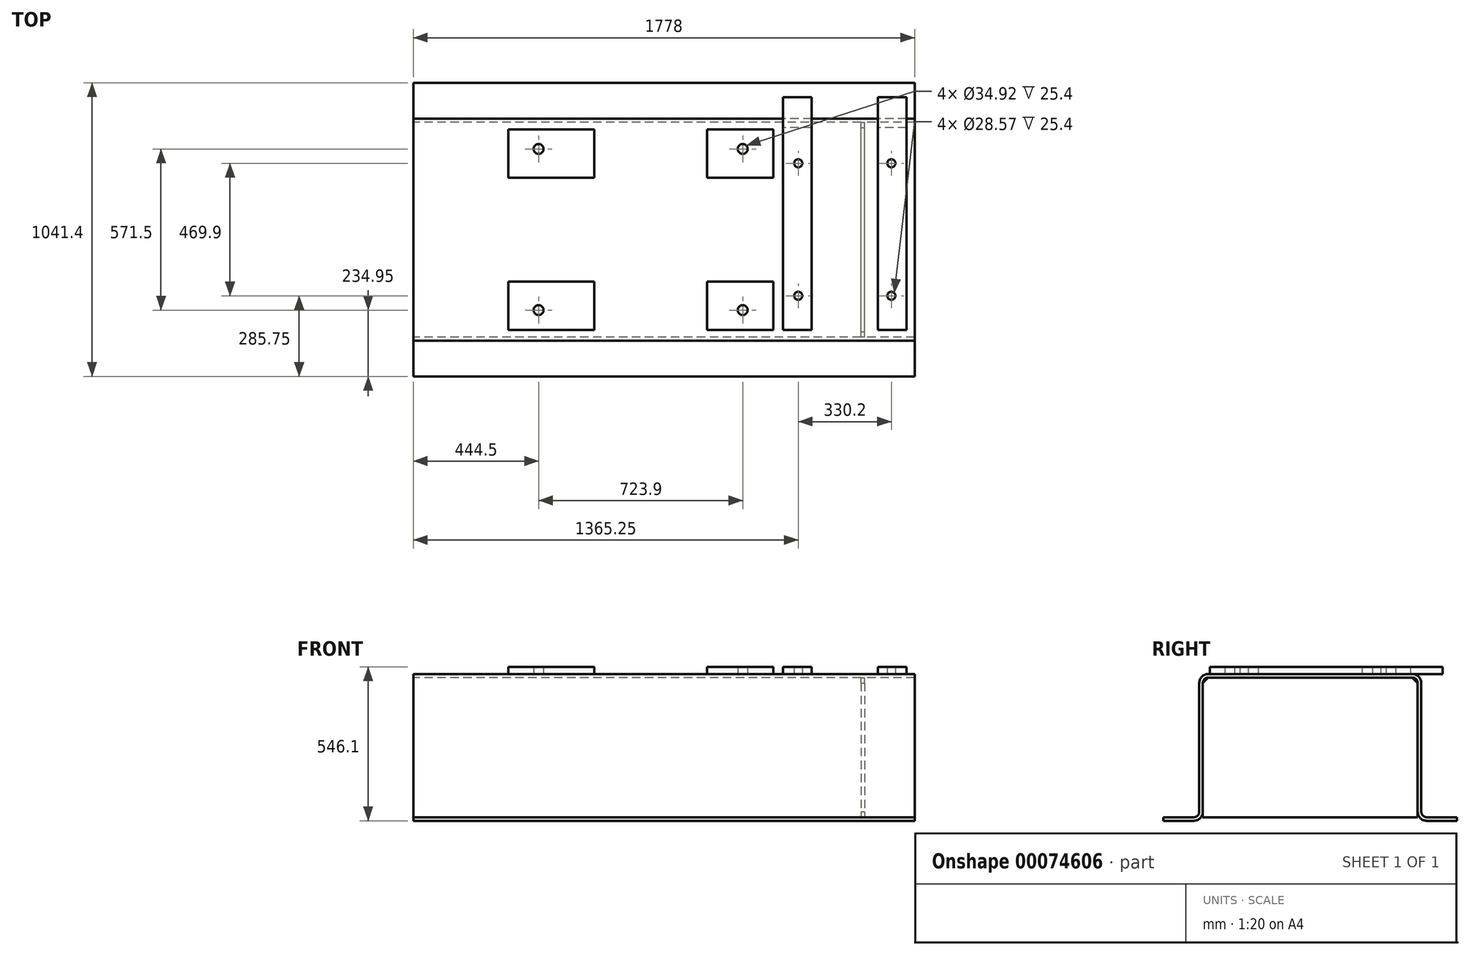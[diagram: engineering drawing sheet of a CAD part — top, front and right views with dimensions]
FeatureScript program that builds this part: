
annotation { "Feature Type Name" : "Feature", "Feature Type Description" : "" }
export const myFeature = defineFeature(function(context is Context, id is Id, definition is map)
    precondition{}
    {
        {
            var Q0;
            Q0=qCreatedBy(makeId("Right.planeOp"),FACE);
            var sketch = newSketch(context, id + "F0", { "sketchPlane" : qUnion([Q0])});
            skLineSegment(sketch, "E0.rect.bottom", {"start": v(-361.95, 260.35) * mm, "end": v(0, 260.35) * mm});
            skLineSegment(sketch, "E0.rect.top", {"start": v(-520.7, -260.35) * mm, "end": v(-412.75, -260.35) * mm});
            skLineSegment(sketch, "E0.rect.left", {"start": v(-393.7, 228.6) * mm, "end": v(-393.7, -228.6) * mm});
            skPoint(sketch, "E0.rect.middle", {"position": v(0, 0) * mm});
            skLineSegment(sketch, "E1", {"start": v(0, 334.43) * mm, "end": v(0, -368.46) * mm, "construction": true});
            skLineSegment(sketch, "E2.0", {"start": v(-520.7, -247.65) * mm, "end": v(-520.7, -260.35) * mm});
            skLineSegment(sketch, "E3.0", {"start": v(-520.7, -247.65) * mm, "end": v(-412.75, -247.65) * mm});
            skLineSegment(sketch, "E4.0", {"start": v(-381, 228.6) * mm, "end": v(-381, -228.6) * mm});
            skLineSegment(sketch, "E5.0", {"start": v(-361.95, 247.65) * mm, "end": v(0, 247.65) * mm});
            skPoint(sketch, "E0.rect.right.end.orphan", {"position": v(393.7, -260.35) * mm});
            skPoint(sketch, "E0.rect.right.start.orphan", {"position": v(393.7, 260.35) * mm});
            skPoint(sketch, "E6.orphan", {"position": v(-393.7, -260.35) * mm});
            skPoint(sketch, "E7.visualSharp", {"position": v(-381, 247.65) * mm});
            skArc(sketch, "E7.filletArc", {"start": v(-361.95, 247.65) * mm, "mid": v(-375.42, 242.07) * mm, "end": v(-381, 228.6) * mm});
            skPoint(sketch, "E8.visualSharp", {"position": v(-393.7, -247.65) * mm});
            skArc(sketch, "E8.filletArc", {"start": v(-412.75, -247.65) * mm, "mid": v(-399.28, -242.07) * mm, "end": v(-393.7, -228.6) * mm});
            skPoint(sketch, "E9.visualSharp", {"position": v(-393.7, 260.35) * mm});
            skArc(sketch, "E9.filletArc", {"start": v(-361.95, 260.35) * mm, "mid": v(-384.4, 251.05) * mm, "end": v(-393.7, 228.6) * mm});
            skPoint(sketch, "E10.visualSharp", {"position": v(-381, -260.35) * mm});
            skArc(sketch, "E10.filletArc", {"start": v(-412.75, -260.35) * mm, "mid": v(-390.3, -251.05) * mm, "end": v(-381, -228.6) * mm});
            skLineSegment(sketch, "E11.MirrorCS", {"start": v(520.7, -247.65) * mm, "end": v(520.7, -260.35) * mm});
            skArc(sketch, "E12.MirrorCS", {"start": v(412.75, -247.65) * mm, "mid": v(399.28, -242.07) * mm, "end": v(393.7, -228.6) * mm});
            skArc(sketch, "E13.MirrorCS", {"start": v(361.95, 247.65) * mm, "mid": v(375.42, 242.07) * mm, "end": v(381, 228.6) * mm});
            skArc(sketch, "E14.MirrorCS", {"start": v(412.75, -260.35) * mm, "mid": v(390.3, -251.05) * mm, "end": v(381, -228.6) * mm});
            skPoint(sketch, "E15.MirrorP", {"position": v(393.7, -247.65) * mm});
            skArc(sketch, "E16.MirrorCS", {"start": v(361.95, 260.35) * mm, "mid": v(384.4, 251.05) * mm, "end": v(393.7, 228.6) * mm});
            skLineSegment(sketch, "E17.MirrorCS", {"start": v(361.95, 260.35) * mm, "end": v(0, 260.35) * mm});
            skLineSegment(sketch, "E18.MirrorCS", {"start": v(520.7, -260.35) * mm, "end": v(412.75, -260.35) * mm});
            skLineSegment(sketch, "E19.MirrorCS", {"start": v(393.7, 228.6) * mm, "end": v(393.7, -228.6) * mm});
            skLineSegment(sketch, "E20.MirrorCS", {"start": v(520.7, -247.65) * mm, "end": v(412.75, -247.65) * mm});
            skPoint(sketch, "E21.MirrorP", {"position": v(381, -260.35) * mm});
            skPoint(sketch, "E22.MirrorP", {"position": v(381, 247.65) * mm});
            skLineSegment(sketch, "E23.MirrorCS", {"start": v(361.95, 247.65) * mm, "end": v(0, 247.65) * mm});
            skLineSegment(sketch, "E24.MirrorCS", {"start": v(381, 228.6) * mm, "end": v(381, -228.6) * mm});
            skSolve(sketch);
        }
        {
            var Q0;
            Q0=qSketchRegion(id+"F0",true);
            extrude(context, id + "F1", {"entities" : qUnion([Q0]), "endBound" : BoundingType.SYMMETRIC, "depth" : 1778 * mm});
        }
        {
            var Q0;
            Q0=makeQuery(id+"F1.opExtrude","SWEPT_FACE",FACE,{"disambiguationData":[OSD([sQuery(id+"F0.wireOp",EDGE,"E0.rect.bottom"),sQuery(id+"F0.wireOp",EDGE,"E17.MirrorCS")])]});
            var sketch = newSketch(context, id + "F2", { "sketchPlane" : qUnion([Q0])});
            skLineSegment(sketch, "E25", {"start": v(-1218.48, 0) * mm, "end": v(1193.9, 0) * mm, "construction": true});
            skLineSegment(sketch, "E26.0", {"start": v(641.35, -361.95) * mm, "end": v(641.35, 361.95) * mm, "construction": true});
            skLineSegment(sketch, "E27.0", {"start": v(-82.55, -361.95) * mm, "end": v(-82.55, 361.95) * mm, "construction": true});
            skLineSegment(sketch, "E28.0", {"start": v(152.4, -361.95) * mm, "end": v(152.4, -184.15) * mm});
            skLineSegment(sketch, "E29.0", {"start": v(387.35, -361.95) * mm, "end": v(387.35, -184.15) * mm});
            skLineSegment(sketch, "E30.0", {"start": v(-247.65, -361.95) * mm, "end": v(-247.65, -184.15) * mm});
            skLineSegment(sketch, "E31.0", {"start": v(-552.45, -361.95) * mm, "end": v(-552.45, -184.15) * mm});
            skLineSegment(sketch, "E32.0", {"start": v(-552.45, -184.15) * mm, "end": v(-247.65, -184.15) * mm});
            skLineSegment(sketch, "E33.0", {"start": v(-552.45, -355.6) * mm, "end": v(-247.65, -355.6) * mm});
            skLineSegment(sketch, "E34.trimOffspring", {"start": v(152.4, -184.15) * mm, "end": v(387.35, -184.15) * mm});
            skLineSegment(sketch, "E35.trimOffspring", {"start": v(152.4, -355.6) * mm, "end": v(387.35, -355.6) * mm});
            skLineSegment(sketch, "E36.0", {"start": v(-1218.48, -285.75) * mm, "end": v(1193.9, -285.75) * mm, "construction": true});
            skLineSegment(sketch, "E37.0", {"start": v(-444.5, -361.95) * mm, "end": v(-444.5, 361.95) * mm, "construction": true});
            skLineSegment(sketch, "E38.0", {"start": v(279.4, -361.95) * mm, "end": v(279.4, 361.95) * mm, "construction": true});
            skCircle(sketch, "E39", {"center": v(-444.5, -285.75) * mm, "radius": 17.46 * mm});
            skCircle(sketch, "E40", {"center": v(279.4, -285.75) * mm, "radius": 17.46 * mm});
            skLineSegment(sketch, "E41.MirrorCS", {"start": v(-552.45, 184.15) * mm, "end": v(-247.65, 184.15) * mm});
            skLineSegment(sketch, "E42.MirrorCS", {"start": v(-552.45, 361.95) * mm, "end": v(-552.45, 184.15) * mm});
            skLineSegment(sketch, "E43.MirrorCS", {"start": v(-247.65, 361.95) * mm, "end": v(-247.65, 184.15) * mm});
            skCircle(sketch, "E44.MirrorC", {"center": v(279.4, 285.75) * mm, "radius": 17.46 * mm});
            skLineSegment(sketch, "E45.MirrorCS", {"start": v(152.4, 355.6) * mm, "end": v(387.35, 355.6) * mm});
            skLineSegment(sketch, "E46.MirrorCS", {"start": v(152.4, 361.95) * mm, "end": v(152.4, 184.15) * mm});
            skCircle(sketch, "E47.MirrorC", {"center": v(-444.5, 285.75) * mm, "radius": 17.46 * mm});
            skLineSegment(sketch, "E48.MirrorCS", {"start": v(387.35, 361.95) * mm, "end": v(387.35, 184.15) * mm});
            skLineSegment(sketch, "E49.MirrorCS", {"start": v(152.4, 184.15) * mm, "end": v(387.35, 184.15) * mm});
            skLineSegment(sketch, "E50.MirrorCS", {"start": v(-552.45, 355.6) * mm, "end": v(-247.65, 355.6) * mm});
            skSolve(sketch);
        }
        {
            var Q0;
            Q0=qSketchRegion(id+"F2",true);
            extrude(context, id + "F3", {"entities" : qUnion([Q0]), "operationType" : NewBodyOperationType.ADD, "depth" : 25.4 * mm});
        }
        {
            var Q0;
            {var subQ20=sQuery(id+"F2.wireOp",EDGE,"E32.0");Q0=makeQuery(id+"F2.imprint","IMPRINT",FACE,{"disambiguationData":[TD([[makeQuery(id+"F2.imprint","IMPRINT",EDGE,{"derivedFrom":subQ20}),1.0]])]});}
            var sketch = newSketch(context, id + "F4", { "sketchPlane" : qUnion([Q0])});
            skLineSegment(sketch, "E51.0", {"start": v(-1218.48, 0) * mm, "end": v(1193.9, 0) * mm, "construction": true});
            skLineSegment(sketch, "E52.0", {"start": v(641.35, -361.95) * mm, "end": v(641.35, 361.95) * mm, "construction": true});
            skLineSegment(sketch, "E53.0", {"start": v(-1218.48, -317.5) * mm, "end": v(1193.9, -317.5) * mm, "construction": true});
            skLineSegment(sketch, "E54.0", {"start": v(-1218.48, 469.9) * mm, "end": v(1193.9, 469.9) * mm, "construction": true});
            skLineSegment(sketch, "E55.0", {"start": v(758.95, -361.95) * mm, "end": v(758.95, 361.95) * mm, "construction": true});
            skLineSegment(sketch, "E56.0", {"start": v(524, -361.95) * mm, "end": v(524, 361.95) * mm, "construction": true});
            skLineSegment(sketch, "E57.0", {"start": v(422.4, -361.95) * mm, "end": v(422.4, 361.95) * mm, "construction": true});
            skLineSegment(sketch, "E58.0", {"start": v(-241.3, -177.8) * mm, "end": v(-241.3, -355.6) * mm, "construction": true});
            skLineSegment(sketch, "E58.1", {"start": v(-558.8, -177.8) * mm, "end": v(-241.3, -177.8) * mm, "construction": true});
            skLineSegment(sketch, "E58.2", {"start": v(-558.8, -355.6) * mm, "end": v(-558.8, -177.8) * mm, "construction": true});
            skLineSegment(sketch, "E58.3", {"start": v(-882.65, -355.6) * mm, "end": v(-558.8, -355.6) * mm, "construction": true});
            skLineSegment(sketch, "E58.4", {"start": v(-882.65, 355.6) * mm, "end": v(-882.65, -355.6) * mm, "construction": true});
            skLineSegment(sketch, "E58.5", {"start": v(-241.3, -355.6) * mm, "end": v(146.05, -355.6) * mm, "construction": true});
            skLineSegment(sketch, "E58.6", {"start": v(-558.8, 355.6) * mm, "end": v(-882.65, 355.6) * mm, "construction": true});
            skLineSegment(sketch, "E58.7", {"start": v(-558.8, 177.8) * mm, "end": v(-558.8, 355.6) * mm, "construction": true});
            skLineSegment(sketch, "E58.8", {"start": v(-241.3, 177.8) * mm, "end": v(-558.8, 177.8) * mm, "construction": true});
            skLineSegment(sketch, "E58.9", {"start": v(-241.3, 355.6) * mm, "end": v(-241.3, 177.8) * mm, "construction": true});
            skLineSegment(sketch, "E58.10", {"start": v(393.7, -355.6) * mm, "end": v(882.65, -355.6) * mm, "construction": true});
            skLineSegment(sketch, "E58.11", {"start": v(393.7, -177.8) * mm, "end": v(393.7, -355.6) * mm, "construction": true});
            skLineSegment(sketch, "E58.12", {"start": v(146.05, -177.8) * mm, "end": v(393.7, -177.8) * mm, "construction": true});
            skLineSegment(sketch, "E58.13", {"start": v(146.05, -355.6) * mm, "end": v(146.05, -177.8) * mm, "construction": true});
            skLineSegment(sketch, "E58.14", {"start": v(882.65, -355.6) * mm, "end": v(882.65, 355.6) * mm, "construction": true});
            skLineSegment(sketch, "E58.15", {"start": v(882.65, 355.6) * mm, "end": v(393.7, 355.6) * mm, "construction": true});
            skLineSegment(sketch, "E58.16", {"start": v(393.7, 355.6) * mm, "end": v(393.7, 177.8) * mm, "construction": true});
            skLineSegment(sketch, "E58.17", {"start": v(393.7, 177.8) * mm, "end": v(146.05, 177.8) * mm, "construction": true});
            skLineSegment(sketch, "E58.18", {"start": v(146.05, 177.8) * mm, "end": v(146.05, 355.6) * mm, "construction": true});
            skLineSegment(sketch, "E58.19", {"start": v(146.05, 355.6) * mm, "end": v(-241.3, 355.6) * mm, "construction": true});
            skLineSegment(sketch, "E59.bottom", {"start": v(422.4, -355.6) * mm, "end": v(524, -355.6) * mm});
            skLineSegment(sketch, "E59.top", {"start": v(422.4, 469.9) * mm, "end": v(524, 469.9) * mm});
            skLineSegment(sketch, "E59.left", {"start": v(422.4, -355.6) * mm, "end": v(422.4, 469.9) * mm});
            skLineSegment(sketch, "E59.right", {"start": v(524, -355.6) * mm, "end": v(524, 469.9) * mm});
            skLineSegment(sketch, "E60.MirrorCS", {"start": v(860.3, -361.95) * mm, "end": v(860.3, 361.95) * mm});
            skLineSegment(sketch, "E61.MirrorCS", {"start": v(758.7, -361.95) * mm, "end": v(758.7, 361.95) * mm});
            skLineSegment(sketch, "E62.MirrorCS", {"start": v(758.7, -355.6) * mm, "end": v(758.7, 469.9) * mm});
            skLineSegment(sketch, "E63.MirrorCS", {"start": v(889, 355.6) * mm, "end": v(889, 177.8) * mm});
            skLineSegment(sketch, "E64.MirrorCS", {"start": v(860.3, -355.6) * mm, "end": v(860.3, 469.9) * mm});
            skLineSegment(sketch, "E65.MirrorCS", {"start": v(860.3, -355.6) * mm, "end": v(758.7, -355.6) * mm});
            skLineSegment(sketch, "E66.MirrorCS", {"start": v(860.3, 469.9) * mm, "end": v(758.7, 469.9) * mm});
            skLineSegment(sketch, "E67.MirrorCS", {"start": v(889, -177.8) * mm, "end": v(889, -355.6) * mm});
            skLineSegment(sketch, "E68.0", {"start": v(-1218.48, -234.95) * mm, "end": v(1193.9, -234.95) * mm, "construction": true});
            skLineSegment(sketch, "E69.0", {"start": v(806.45, -361.95) * mm, "end": v(806.45, 361.95) * mm, "construction": true});
            skCircle(sketch, "E70", {"center": v(806.45, -234.95) * mm, "radius": 14.29 * mm});
            skCircle(sketch, "E71.MirrorC", {"center": v(476.25, -234.95) * mm, "radius": 14.29 * mm});
            skCircle(sketch, "E72.MirrorC", {"center": v(476.25, 234.95) * mm, "radius": 14.29 * mm});
            skCircle(sketch, "E73.MirrorC", {"center": v(806.45, 234.95) * mm, "radius": 14.29 * mm});
            skSolve(sketch);
        }
        {
            var Q0;
            Q0=qSketchRegion(id+"F4",true);
            extrude(context, id + "F5", {"entities" : qUnion([Q0]), "operationType" : NewBodyOperationType.ADD, "depth" : 25.4 * mm});
        }
        {
            var Q0;
            Q0=makeQuery(id+"F1.opExtrude","CAP_FACE",FACE,{"disambiguationData":[OSD([sQuery(id+"F0.wireOp",EDGE,"E0.rect.bottom"),sQuery(id+"F0.wireOp",EDGE,"E0.rect.top"),sQuery(id+"F0.wireOp",EDGE,"E0.rect.left"),sQuery(id+"F0.wireOp",EDGE,"E2.0"),sQuery(id+"F0.wireOp",EDGE,"E3.0"),sQuery(id+"F0.wireOp",EDGE,"E4.0"),sQuery(id+"F0.wireOp",EDGE,"E5.0"),sQuery(id+"F0.wireOp",EDGE,"E7.filletArc"),sQuery(id+"F0.wireOp",EDGE,"E8.filletArc"),sQuery(id+"F0.wireOp",EDGE,"E9.filletArc"),sQuery(id+"F0.wireOp",EDGE,"E10.filletArc"),sQuery(id+"F0.wireOp",EDGE,"E11.MirrorCS"),sQuery(id+"F0.wireOp",EDGE,"E12.MirrorCS"),sQuery(id+"F0.wireOp",EDGE,"E13.MirrorCS"),sQuery(id+"F0.wireOp",EDGE,"E14.MirrorCS"),sQuery(id+"F0.wireOp",EDGE,"E16.MirrorCS"),sQuery(id+"F0.wireOp",EDGE,"E17.MirrorCS"),sQuery(id+"F0.wireOp",EDGE,"E18.MirrorCS"),sQuery(id+"F0.wireOp",EDGE,"E19.MirrorCS"),sQuery(id+"F0.wireOp",EDGE,"E20.MirrorCS"),sQuery(id+"F0.wireOp",EDGE,"E23.MirrorCS"),sQuery(id+"F0.wireOp",EDGE,"E24.MirrorCS")])],"isStart":false});
            cPlane(context, id + "F6", {"entities" : qUnion([Q0]), "cplaneType" : CPlaneType.OFFSET, "offset" : 177.8 * mm, "oppositeDirection" : true, "width" : 152.4 * mm, "height" : 152.4 * mm});
        }
        {
            var Q0;
            Q0=qCreatedBy(id+"F6.planeOp",FACE);
            var sketch = newSketch(context, id + "F7", { "sketchPlane" : qUnion([Q0])});
            skLineSegment(sketch, "E74.0", {"start": v(-381, 228.6) * mm, "end": v(-381, -247.65) * mm});
            skLineSegment(sketch, "E75.0", {"start": v(-361.95, 247.65) * mm, "end": v(361.95, 247.65) * mm});
            skLineSegment(sketch, "E76.0", {"start": v(381, 228.6) * mm, "end": v(381, -247.65) * mm});
            skLineSegment(sketch, "E77.0", {"start": v(-520.7, -247.65) * mm, "end": v(-412.75, -247.65) * mm, "construction": true});
            skLineSegment(sketch, "E78", {"start": v(-412.75, -247.65) * mm, "end": v(389.6, -247.65) * mm});
            skLineSegment(sketch, "E79", {"start": v(-381, 228.6) * mm, "end": v(-361.95, 247.65) * mm});
            skLineSegment(sketch, "E80", {"start": v(361.95, 247.65) * mm, "end": v(381, 228.6) * mm});
            skPoint(sketch, "E81.orphan", {"position": v(-381, -228.6) * mm});
            skPoint(sketch, "E82.orphan", {"position": v(381, -228.6) * mm});
            skSolve(sketch);
        }
        {
            var Q0;
            Q0=qSketchRegion(id+"F7",true);
            extrude(context, id + "F8", {"entities" : qUnion([Q0]), "operationType" : NewBodyOperationType.ADD, "oppositeDirection" : true, "depth" : 12.7 * mm});
        }
    });
